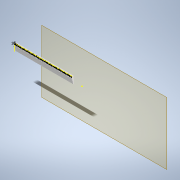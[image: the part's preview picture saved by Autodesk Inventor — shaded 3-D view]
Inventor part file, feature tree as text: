
AUTODESK INVENTOR PART (.ipt)
format: ipt  version: 2021 (Build 250183000, 183)  size: 411,136 bytes
history: native  units: mm
features: sketch x3, other x2, extrude x2, chamfer x1, pattern_linear x1
ambient origin geometry x8: Origin, YZ Plane, XZ Plane, XY Plane, X Axis, Y Axis, Z Axis, Center Point
bodies: Body1 (feature_tree), Body2 (feature_tree)
feature tree (9):
  other  "Bryła1"
  other  "Płaszczyzna konstrukcyjna1"
  extrude  "Wyciągnięcie proste1"  Depth=400.0mm
  chamfer  "Faza1"  Distance=50.0mm
  sketch  "Szkic2"
  extrude  "Wyciągnięcie proste2"  Depth=10.0mm TaperAngle=0.0deg
  pattern_linear  "Szyk prostokątny1"  Spacing1=34.0mm  [1 undecoded]
  sketch  "Szkic1"
  sketch  "Szkic3"
note: 1 required parameter value undecoded (feature->parameter linkage not recoverable at this tier; creation-order binding heuristic only, values carry confidence <= 0.55)
